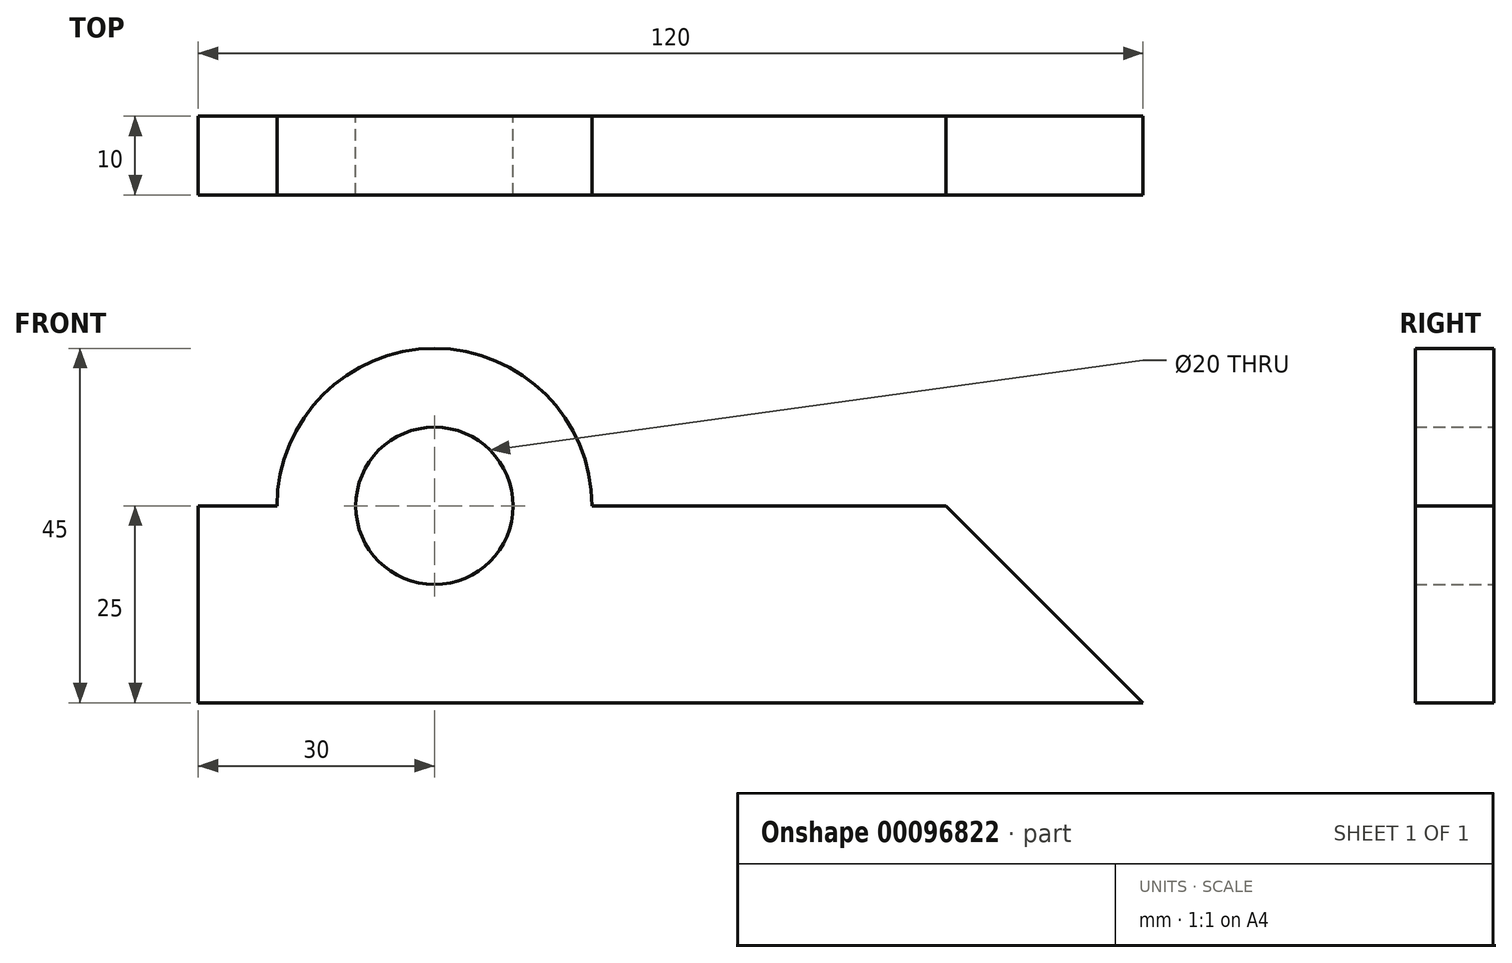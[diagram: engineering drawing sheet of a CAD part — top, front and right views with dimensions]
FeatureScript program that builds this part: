
annotation { "Feature Type Name" : "Feature", "Feature Type Description" : "" }
export const myFeature = defineFeature(function(context is Context, id is Id, definition is map)
    precondition{}
    {
        {
            var Q0;
            Q0=qCreatedBy(makeId("Front.planeOp"),FACE);
            var sketch = newSketch(context, id + "F0", { "sketchPlane" : qUnion([Q0])});
            skLineSegment(sketch, "E0", {"start": v(0, 0) * mm, "end": v(120, 0) * mm});
            skLineSegment(sketch, "E1", {"start": v(120, 0) * mm, "end": v(95, 25) * mm});
            skLineSegment(sketch, "E2", {"start": v(0, 0) * mm, "end": v(0, 25) * mm});
            skCircle(sketch, "E3", {"center": v(30, 25) * mm, "radius": 10 * mm});
            skArc(sketch, "E4", {"start": v(10, 25) * mm, "mid": v(30, 45) * mm, "end": v(50, 25) * mm});
            skLineSegment(sketch, "E5", {"start": v(10, 25) * mm, "end": v(0, 25) * mm});
            skLineSegment(sketch, "E6", {"start": v(50, 25) * mm, "end": v(95, 25) * mm});
            skSolve(sketch);
        }
        {
            var Q0;
            Q0 = qSketchRegion(id + "F0", true);
            extrude(context, id + "F1", {"entities" : qUnion([Q0]), "depth" : 10 * mm});
        }
    });
